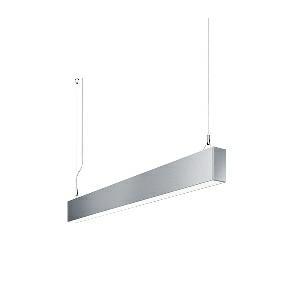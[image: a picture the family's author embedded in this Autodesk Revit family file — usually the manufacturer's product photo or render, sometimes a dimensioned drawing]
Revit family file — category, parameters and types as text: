
# Revit family: idoo_line_-_ilp_2000_vtl_d_00806460_a8f3
name_source: partatom
category: Lighting Fixtures
units: mm (PartAtom-declared; Revit-internal decimal feet)

## family parameters
Cut with Voids When Loaded = No
Host = Face
Light Source = No
Part Type = Normal
Room Calculation Point = No
Round Connector Dimension = Use Diameter
Shared = No

## types (1)
- IDOO.line - ILP 2000/VTL/D (1 x LED, 2300 lm, 2700-6500K)
    Apparent Load = 23 VA
    Approval mark = CE
    CIE Flux Codes = 66 91 98 40 100
    Color Rendering = 90-100
    Color Temperature = 2700-6500K
    Control Gear = Electronic ballast
    Default Elevation = 1800 mm
    Description = ILP 2000/VTL/D|Suspended luminaire|light source: LED|connected load: 220-240 V, 50/60 Hz|Power consumption: approx. 23 W|standby: approx. 0,25|luminous flux: 2300 lm|luminous efficacy: 100 lm/W|light distribution: Direct/indirect|direct ratio: approx. 40 %|colour temperature: Cold white, ca. 2700-6500 K|color rendering index (CRI): >= 90|chromaticity tolerance:  3 SDCM|System of protection: IP 40|technology: Continuously dimmable|luminaire body|material: Sectional aluminium|colour: Silver|lamp cover: Acrylic (PMMA), Clear|mains lead: 2.00 m With free stranded wires|Fastening: Steel cable 0.3 - 0.7 m|glare control: Prism aperture|luminance(L65): <= 2700 cd/m|unified glare rating(4H 8H): <=  16|special features: Specified values at approx. 4000 K, DALI Load 1x, External control required for Dali Device type 8, Flicker-free, Constant luminous flux between 2700 and 6500 K, Constant colour temperature over the whole dimming range, Suitable as emergency lighting|
    Frequency = 50 Hz
    Height = 110 mm
    Lamp = 1 x LED
    Lamp Light Flux = 2300 lm
    Lamp count = 1
    Length = 854 mm
    Luminous efficacy = 100 lm/W
    Manufacturer = Waldmann
    ModVariant = No
    Model = 00806460
    Mounting Place = Ceiling
    Mounting Type = Pendant
    Number of Poles = 1
    OnlyDefault = Yes
    Power Factor = 1
    Product Name = IDOO.line - ILP 2000/VTL/D
    Product group = Suspended luminaire
    ProductGroupID = 9
    Protection Class = Protection class I
    Protection Degree = IP 40
    RLX_Detail_Level = 1
    RLX_Emergency_Light_Flux = 0 lm
    RLX_Emergency_Type = 0
    RLX_Emergency_Type_DB = No
    RlxData = <blob elided: 19925 chars, md5=db785ffd>
    Socket = socket
    Standby Power = 0 W
    System Light Flux = 2300 lm
    System Power = 23 W
    Type Comments = Product without accessories
    Type Image = 113288000-00692512.jpg
    URL = http://relux.com
    VarID = ---
    Voltage = 230 V
    Voltage Range = 220-240 V
    Weight = 0.00 kg
    Width = 60 mm  [stored 0.19685 ft]

note: [stored X ft] marks values corroborated as IEEE doubles in the binary element streams (Revit-internal decimal feet)

## geometry (parser evidence)
native form markers: Blend x4, Sweep x14
no freeform markers — native parametric forms only
